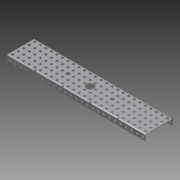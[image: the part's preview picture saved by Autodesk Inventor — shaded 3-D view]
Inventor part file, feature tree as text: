
AUTODESK INVENTOR PART (.ipt)
format: ipt  version: 2012 (Build 160160000, 160)  size: 2,039,808 bytes
history: native  units: in
note: dims shown in document units (in); Inventor stores cm internally (conversion verified against a paired STEP export)
features: hole x2, sketch x2, other x1, imported_body x1
ambient origin geometry x8: Origin, YZ Plane, XZ Plane, XY Plane, X Axis, Y Axis, Z Axis, Center Point
feature tree (6):
  parser-record x1  (decoder bookkeeping rows leaked as tree rows — omitted from the tree; the rows remain in map.json)
  imported_body  "Base1"
  hole  "Hole1"  [1 undecoded]
  hole  "Hole4"  [1 undecoded]
  sketch  "Sketch1"  dims[d0=0.7in]
  sketch  "Sketch4"  dims[d1=0.7in d2=0.75in d3=0.375in d4=0.25in d5=0.5635in d6=1.0in d7=0.8108in d24=0.3125in d25=0.3125in d26=0.3125in d27=0.75in d28=0.375in d29=0.25in d30=0.5635in d31=1.0in d32=0.8108in]
note: 2 required parameter values undecoded (feature->parameter linkage not recoverable at this tier; creation-order binding heuristic only, values carry confidence <= 0.55)
